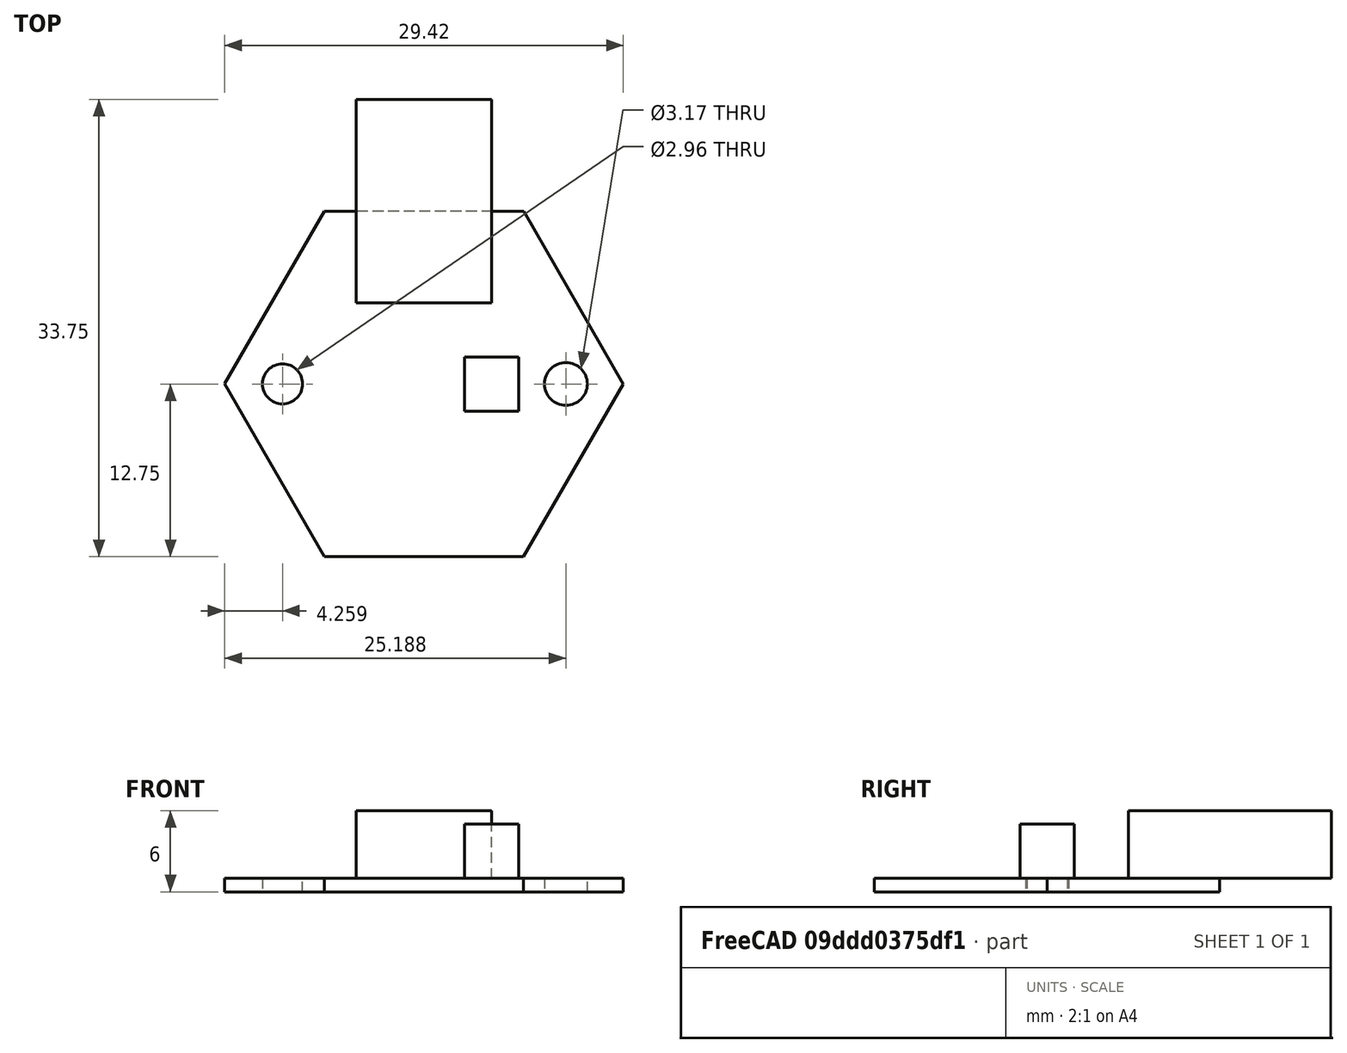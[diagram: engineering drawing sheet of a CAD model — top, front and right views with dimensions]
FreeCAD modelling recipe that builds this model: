
FCSTD DOCUMENT  (FreeCAD 0.19R24291 (Git))
Label: infrarrojos
License: All rights reserved
LicenseURL: http://en.wikipedia.org/wiki/All_rights_reserved
objects: Part::Box×2, Sketcher::SketchObject×1, PartDesign::Pad×1, PartDesign::Body×1
note: 6 computed .brp shape members not serialized (recipe doc carries the construction recipe); baked Part::Feature solids carry a one-line shape summary decoded from their .brp

FEATURE [Sketcher::SketchObject] Sketch
  FullyConstrained = false
  MapMode = 5
  Support = -> [XY_Plane]
  sketch-geometry (9):
    g0: LineSegment StartX=7.36377 StartY=12.7393 StartZ=0 EndX=-7.35069 EndY=12.7469 EndZ=0
    g1: LineSegment StartX=-7.35069 StartY=12.7469 StartZ=0 EndX=-14.7145 EndY=0.00755112 EndZ=0
    g2: LineSegment StartX=-14.7145 StartY=0.00755112 StartZ=0 EndX=-7.36377 EndY=-12.7393 EndZ=0
    g3: LineSegment StartX=-7.36377 StartY=-12.7393 StartZ=0 EndX=7.35069 EndY=-12.7469 EndZ=0
    g4: LineSegment StartX=7.35069 StartY=-12.7469 StartZ=0 EndX=14.7145 EndY=-0.00755112 EndZ=0
    g5: LineSegment StartX=14.7145 StartY=-0.00755112 StartZ=0 EndX=7.36377 EndY=12.7393 EndZ=0
    g6: Circle CenterX=0 CenterY=0 CenterZ=0 NormalX=0 NormalY=0 NormalZ=1 AngleXU=0 Radius=14.7145
    g7: Circle CenterX=-10.4508 CenterY=0 CenterZ=0 NormalX=0 NormalY=0 NormalZ=1 AngleXU=0 Radius=1.48082
    g8: Circle CenterX=10.4782 CenterY=0 CenterZ=0 NormalX=0 NormalY=0 NormalZ=1 AngleXU=0 Radius=1.58263
  constraints (16):
    c: Coincident(g0,g1)
    c: Coincident(g1,g2)
    c: Coincident(g2,g3)
    c: Coincident(g3,g4)
    c: Coincident(g4,g5)
    c: Coincident(g5,g0)
    c: Equal(g0, g1-g5) x5
    c: PointOnObject(g0,g6)
    c: PointOnObject(g1,g6)
    c: PointOnObject(g2,g6)
    c: PointOnObject(g3,g6)
    c: PointOnObject(g4,g6)
    c: PointOnObject(g5,g6)
    c: Coincident(g6,g-1)
    c: PointOnObject(g7,g-1)
    c: PointOnObject(g8,g-1)
FEATURE [PartDesign::Pad] Pad
  Direction = (1,1,1)
  Length = 1
  Length2 = 100
  Profile = -> Sketch
  Type = 0
FEATURE [PartDesign::Body] Body  label="Body_hexagon"
  Group = -> [Sketch,Pad]
  Origin = -> Origin
  Tip = -> Pad
FEATURE [Part::Box] Box  label="Vcc"
  AttacherType = Attacher::AttachEngine3D
  Height = 5
  Length = 10
  Placement = pos=(-5,6,1) rot=(0,0,1;0rad)
  Width = 15
FEATURE [Part::Box] Box001  label="Elemento1"
  AttacherType = Attacher::AttachEngine3D
  Height = 4
  Length = 4
  Placement = pos=(3,-2,1) rot=(0,0,1;0rad)
  Width = 4
